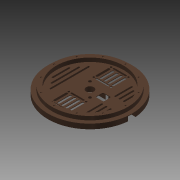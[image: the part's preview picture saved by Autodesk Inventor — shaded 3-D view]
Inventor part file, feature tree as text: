
AUTODESK INVENTOR PART (.ipt)
format: ipt  version: 2015 (Build 190159000, 159)  size: 552,960 bytes
history: native  units: in
note: dims shown in document units (in); Inventor stores cm internally (conversion verified against a paired STEP export)
features: sketch x12, extrude x11, projected_geometry x6, fillet x1
ambient origin geometry x8: Origin, YZ Plane, XZ Plane, XY Plane, X Axis, Y Axis, Z Axis, Center Point
bodies: Solid1 (feature_tree)
feature tree (30):
  extrude  "Extrusion1"  Depth=0.6299in TaperAngle=0.0deg
  extrude  "Extrusion2"  Depth=4.8819in
  extrude  "Extrusion3"  Depth=0.7874in
  sketch  "Sketch4"  dims[d8=0.1969in d9=0.0in d10=0.1181in d11=5.1969in]
  extrude  "Extrusion4"  Depth=0.1181in
  fillet  "Fillet1"  Radius=5.1969in
  extrude  "Extrusion5"  Depth=0.0591in TaperAngle=0.0deg
  extrude  "Extrusion6"  Depth=1.6535in
  extrude  "Extrusion7"  Depth=0.7087in
  extrude  "Extrusion8"  Depth=0.0787in
  extrude  "Extrusion9"  Depth=0.1575in
  extrude  "Extrusion10"  Depth=0.315in
  extrude  "Extrusion11"  Depth=0.1575in
  sketch  "Sketch1"  dims[d0=6.1024in d1=0.6299in d2=0.0in]
  sketch  "Sketch2"  dims[d3=5.5118in d4=4.8819in]
  projected_geometry  "Projected Loop1"
  sketch  "Sketch3"  dims[d5=0.2756in d6=0.0in d7=0.7874in]
  sketch  "Sketch5"  dims[d12=4.7244in d14=360.0deg d16=0.0591in d17=0.0in]
  projected_geometry  "Projected Loop2"
  sketch  "Sketch6"  dims[d18=0.0591in d19=1.6535in]
  sketch  "Sketch7"  dims[d20=1.6535in d21=0.7087in]
  projected_geometry  "Projected Loop3"
  sketch  "Sketch8"  dims[d22=0.8268in d23=0.0787in]
  sketch  "Sketch9"  dims[d24=0.315in d25=0.0in d26=0.1575in]
  projected_geometry  "Projected Loop4"
  sketch  "Sketch10"  dims[d27=0.8661in d28=0.315in]
  sketch  "Sketch11"  dims[d29=0.315in d30=0.1575in]
  projected_geometry  "Projected Loop5"
  sketch  "Sketch12"  dims[d31=1.9685in d33=0.2953in d34=0.3937in d36=0.3937in d38=0.315in d39=0.0in d40=0.5512in d41=0.5906in d42=0.0in d43=45.0deg d44=45.0deg d45=0.1969in d46=0.1969in d47=0.315in d48=0.0in d49=45.0deg d50=1.5748in d52=360.0deg d54=3.6883in d55=45.0deg d56=45.0deg d57=0.1969in d58=0.1969in d59=0.1181in d60=0.5906in d61=2.7559in d62=0.1181in d63=0.4724in d64=0.0in d72=0.4724in d73=1.1811in d74=0.9843in d75=0.1181in d76=0.1181in d77=0.315in d78=0.315in d79=1.9685in d80=1.1811in d81=0.1181in d82=0.1181in d83=0.315in d84=0.315in d85=0.9843in d86=0.7874in d87=0.0in d88=45.0deg d89=0.2047in d90=0.2047in d91=0.7185in d92=0.7185in d93=0.4724in d94=0.0in d95=0.1378in d96=0.1378in d97=1.2598in d98=0.1378in d99=0.1378in d100=1.2598in d101=0.1969in d102=0.1969in d103=1.2598in d104=0.1969in d105=0.1181in d106=0.8661in d107=0.6693in d108=0.0787in d109=0.4724in d110=0.0in d111=0.5906in]
  projected_geometry  "Projected Loop6"
